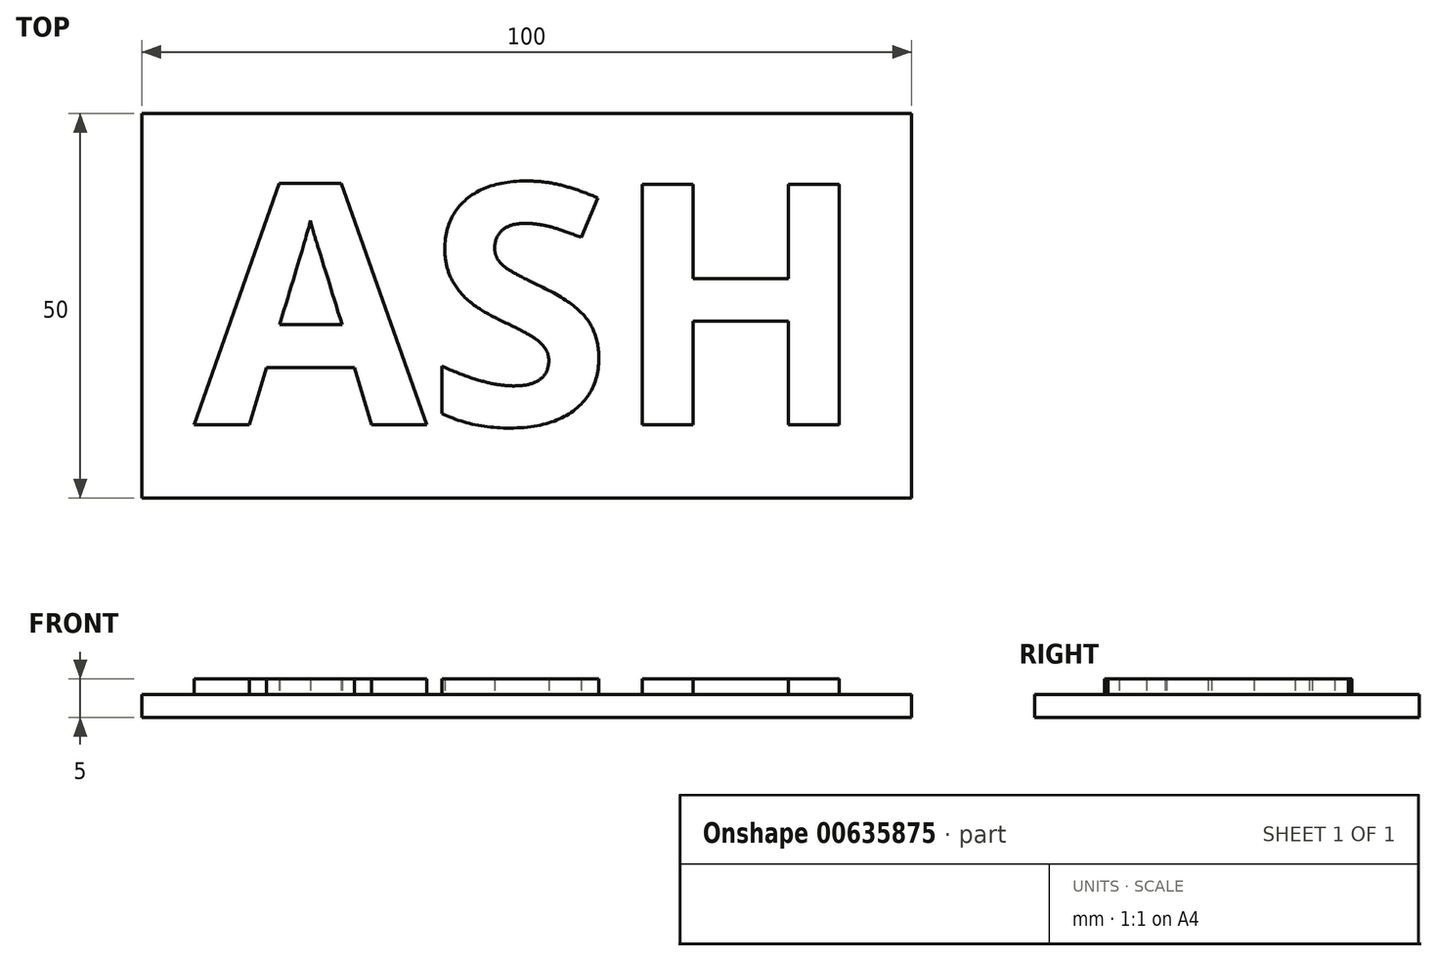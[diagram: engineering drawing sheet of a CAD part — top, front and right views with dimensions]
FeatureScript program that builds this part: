
annotation { "Feature Type Name" : "Feature", "Feature Type Description" : "" }
export const myFeature = defineFeature(function(context is Context, id is Id, definition is map)
    precondition{}
    {
        {
            var Q0;
            Q0=qCreatedBy(makeId("Top.planeOp"),FACE);
            var sketch = newSketch(context, id + "F0", { "sketchPlane" : qUnion([Q0])});
            skLineSegment(sketch, "E0.bottom", {"start": v(0, 0) * mm, "end": v(100, 0) * mm});
            skLineSegment(sketch, "E0.top", {"start": v(0, 50) * mm, "end": v(100, 50) * mm});
            skLineSegment(sketch, "E0.left", {"start": v(0, 0) * mm, "end": v(0, 50) * mm});
            skLineSegment(sketch, "E0.right", {"start": v(100, 0) * mm, "end": v(100, 50) * mm});
            skSolve(sketch);
        }
        {
            var Q0;
            Q0 = qSketchRegion(id + "F0", true);
            extrude(context, id + "F1", {"entities" : qUnion([Q0]), "depth" : 3 * mm, "offsetDistance" : 25 * mm});
        }
        {
            var Q0;
            Q0=makeQuery(id+"F1.opExtrude","CAP_FACE",FACE,{"disambiguationData":[OSD([sQuery(id+"F0.wireOp",EDGE,"E0.bottom"),sQuery(id+"F0.wireOp",EDGE,"E0.top"),sQuery(id+"F0.wireOp",EDGE,"E0.left"),sQuery(id+"F0.wireOp",EDGE,"E0.right")])],"isStart":false});
            var sketch = newSketch(context, id + "F2", { "sketchPlane" : qUnion([Q0])});
            skText(sketch, "E1", { "text": "Mrs G", "fontName": "OpenSans-BoldItalic.ttf"});
            const initialGuessF2  = {"E1": [0.00908, 0.0154, 1, 0, 0.02074]};
            skSetInitialGuess(sketch, initialGuessF2);
            skSolve(sketch);
        }
        {
            var Q0;
            Q0 = qSketchRegion(id + "F2", true);
            var Q1;
            Q1=makeQuery(id+"F2.imprint","IMPRINT",FACE,{"disambiguationData":[TD([[makeQuery(id+"F2.imprint","IMPRINT",EDGE,{"derivedFrom":sQuery(id+"F2.wireOp",EDGE,"E1.sketch_text.stroke-0")}),1.0]])]});
            extrude(context, id + "F3", {"entities" : qUnion([Q0, Q1]), "operationType" : NewBodyOperationType.ADD, "depth" : -1 * mm, "offsetDistance" : 25 * mm});
        }
        {
            var Q0;
            Q0=makeQuery(id+"F1.opExtrude","CAP_FACE",FACE,{"disambiguationData":[OSD([sQuery(id+"F0.wireOp",EDGE,"E0.bottom"),sQuery(id+"F0.wireOp",EDGE,"E0.top"),sQuery(id+"F0.wireOp",EDGE,"E0.left"),sQuery(id+"F0.wireOp",EDGE,"E0.right")])],"isStart":false});
            var sketch = newSketch(context, id + "F4", { "sketchPlane" : qUnion([Q0])});
            skText(sketch, "E2", { "text": "ASH", "fontName": "OpenSans-Bold.ttf"});
            const initialGuessF4  = {"E2": [0.00681, 0.00954, 1, 0, 0.0315]};
            skSetInitialGuess(sketch, initialGuessF4);
            skSolve(sketch);
        }
        {
            var Q0;
            Q0 = qSketchRegion(id + "F4", true);
            extrude(context, id + "F5", {"entities" : qUnion([Q0]), "operationType" : NewBodyOperationType.ADD, "depth" : -1 * mm, "offsetDistance" : 25 * mm});
        }
        {
            var Q0;
            Q0 = qSketchRegion(id + "F4", true);
            extrude(context, id + "F6", {"entities" : qUnion([Q0]), "operationType" : NewBodyOperationType.ADD, "depth" : 2 * mm, "offsetDistance" : 25 * mm});
        }
    });
